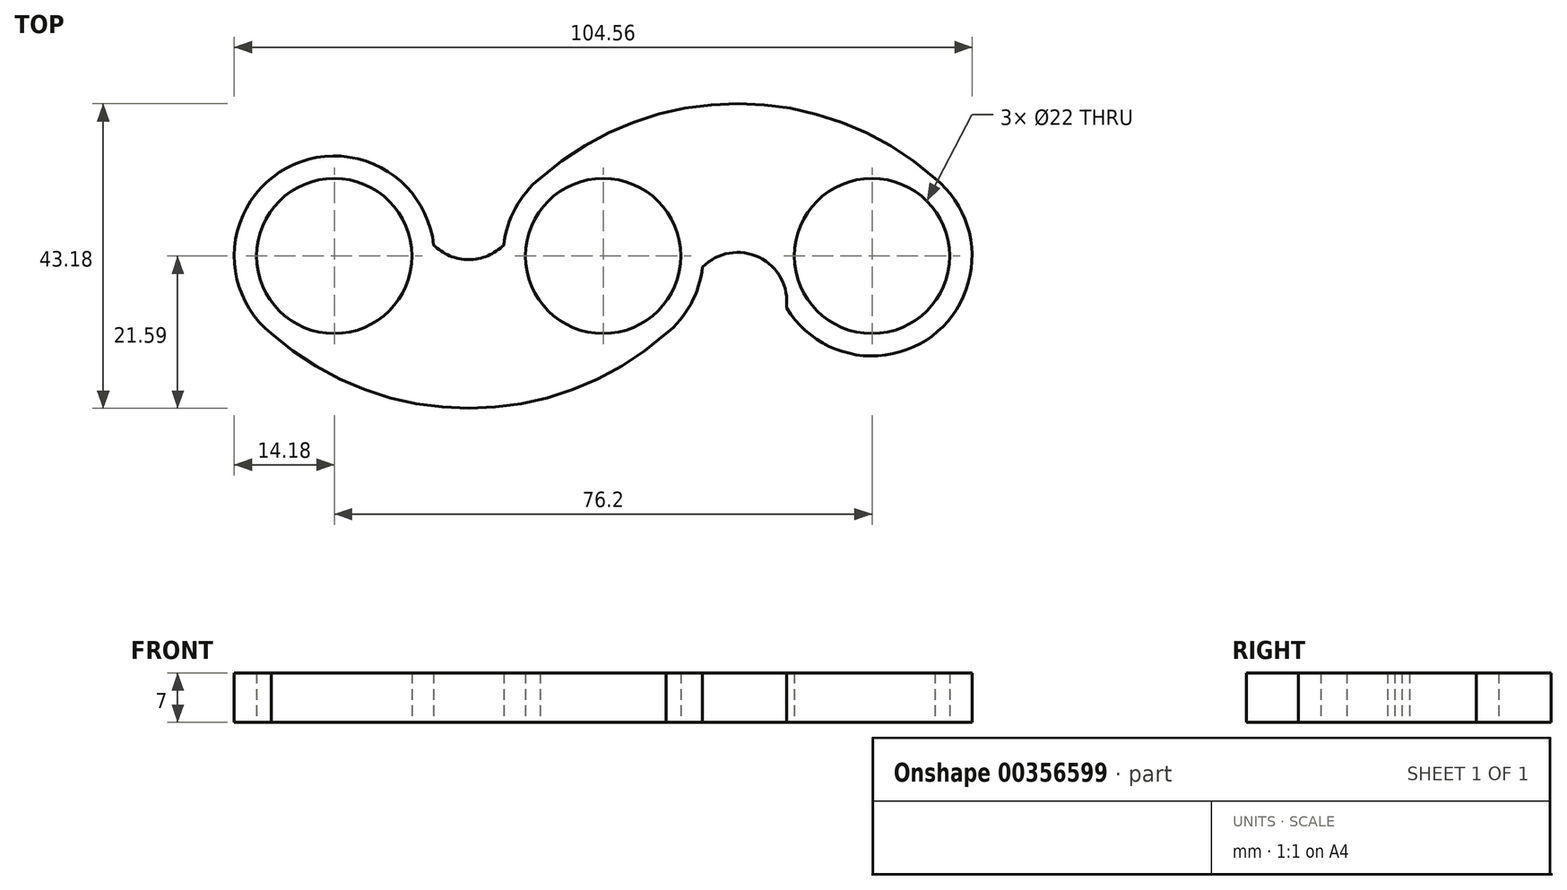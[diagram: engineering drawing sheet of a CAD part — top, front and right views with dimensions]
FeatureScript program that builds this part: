
annotation { "Feature Type Name" : "Feature", "Feature Type Description" : "" }
export const myFeature = defineFeature(function(context is Context, id is Id, definition is map)
    precondition{}
    {
        {
            var Q0;
            Q0=qCreatedBy(makeId("Top.planeOp"),FACE);
            var sketch = newSketch(context, id + "F0", { "sketchPlane" : qUnion([Q0])});
            skCircle(sketch, "E0", {"center": v(0, 0) * mm, "radius": 11 * mm});
            skLineSegment(sketch, "E1", {"start": v(0, 0) * mm, "end": v(-38.1, 0) * mm});
            skLineSegment(sketch, "E2", {"start": v(0, 0) * mm, "end": v(38.1, 0) * mm});
            skCircle(sketch, "E3", {"center": v(-38.1, 0) * mm, "radius": 11 * mm});
            skCircle(sketch, "E4", {"center": v(38.1, 0) * mm, "radius": 11 * mm});
            skCircle(sketch, "E5", {"center": v(-38.1, 0) * mm, "radius": 14.17 * mm});
            skCircle(sketch, "E6", {"center": v(38.1, 0) * mm, "radius": 14.17 * mm});
            skCircle(sketch, "E7", {"center": v(0, 0) * mm, "radius": 14.17 * mm});
            skPoint(sketch, "E8", {"position": v(0, 14.17) * mm});
            skPoint(sketch, "E9", {"position": v(-50.8, 6.3) * mm});
            skPoint(sketch, "E10", {"position": v(-29.16, 11) * mm});
            skPoint(sketch, "E11", {"position": v(-8.94, 11) * mm});
            skPoint(sketch, "E12", {"position": v(-25.97, 7.33) * mm});
            skPoint(sketch, "E13", {"position": v(-12.13, 7.33) * mm});
            skPoint(sketch, "E14", {"position": v(-16.43, 0) * mm});
            skPoint(sketch, "E15", {"position": v(-47.04, -11) * mm});
            skPoint(sketch, "E16", {"position": v(8.94, -11) * mm});
            skPoint(sketch, "E17", {"position": v(-16.44, -21.5) * mm});
            skArc(sketch, "E18", {"start": v(-47.04, -11) * mm, "mid": v(-19.05, -21.59) * mm, "end": v(8.94, -11) * mm});
            skLineSegment(sketch, "E19", {"start": v(0, 55.32) * mm, "end": v(0, -62.03) * mm});
            skPoint(sketch, "E20", {"position": v(16.43, 0) * mm});
            skPoint(sketch, "E21", {"position": v(25.97, -7.34) * mm});
            skPoint(sketch, "E22", {"position": v(12.13, -7.34) * mm});
            skPoint(sketch, "E23", {"position": v(47.04, 11) * mm});
            skPoint(sketch, "E24", {"position": v(16.43, 21.51) * mm});
            skArc(sketch, "E25", {"start": v(47.04, 11) * mm, "mid": v(19.05, 21.6) * mm, "end": v(-8.94, 11) * mm});
            skArc(sketch, "E26", {"start": v(25.97, -7.34) * mm, "mid": v(19.05, 0.5) * mm, "end": v(12.13, -7.34) * mm});
            skArc(sketch, "E27", {"start": v(-25.97, 7.33) * mm, "mid": v(-19.05, -0.5) * mm, "end": v(-12.13, 7.33) * mm});
            skSolve(sketch);
        }
        {
            var Q0;
            Q0=makeQuery(id+"F0.imprint","IMPRINT",FACE,{"disambiguationData":[TD([[makeQuery(id+"F0.imprint","IMPRINT",EDGE,{"derivedFrom":sQuery(id+"F0.wireOp",EDGE,"E4")}),-1.0]])]});
            var Q1;
            {var subQ1=sQuery(id+"F0.wireOp",EDGE,"E2");var subQ5=sQuery(id+"F0.wireOp",EDGE,"E26");var subQ6=makeQuery(id+"F0.imprint","INTERSECT",VERTEX,{"disambiguationData":[OD(0.0)],"derivedFrom":[subQ1,subQ5]});Q1=makeQuery(id+"F0.imprint","IMPRINT",FACE,{"disambiguationData":[TD([[makeQuery(id+"F0.imprint","IMPRINT",EDGE,{"disambiguationData":[TD([[subQ6,1.0]])],"derivedFrom":subQ1}),1.0]])]});}
            var Q2;
            {var subQ1=sQuery(id+"F0.wireOp",EDGE,"E1");var subQ9=sQuery(id+"F0.wireOp",EDGE,"hHHfzR90-xdfu-g8HF-ednO-0jAwHizbKKlp");var subQ12=makeQuery(id+"F0.imprint","INTERSECT",VERTEX,{"disambiguationData":[OD(0.0)],"derivedFrom":[subQ1,subQ9]});Q2=makeQuery(id+"F0.imprint","IMPRINT",FACE,{"disambiguationData":[TD([[makeQuery(id+"F0.imprint","IMPRINT",EDGE,{"disambiguationData":[TD([[subQ12,1.0]])],"derivedFrom":subQ1}),1.0]])]});}
            var Q3;
            Q3=makeQuery(id+"F0.imprint","IMPRINT",FACE,{"disambiguationData":[TD([[makeQuery(id+"F0.imprint","IMPRINT",EDGE,{"derivedFrom":sQuery(id+"F0.wireOp",EDGE,"E3")}),-1.0]])]});
            var Q4;
            {var subQ6=sQuery(id+"F0.wireOp",EDGE,"E2");var subQ7=sQuery(id+"F0.wireOp",EDGE,"E0");var subQ8=makeQuery(id+"F0.imprint","INTERSECT",VERTEX,{"derivedFrom":[subQ7,subQ6]});Q4=makeQuery(id+"F0.imprint","IMPRINT",FACE,{"disambiguationData":[TD([[makeQuery(id+"F0.imprint","IMPRINT",EDGE,{"disambiguationData":[TD([[subQ8,1.0]])],"derivedFrom":subQ7}),-1.0]])]});}
            var Q5;
            {var subQ0=sQuery(id+"F0.wireOp",EDGE,"E1");var subQ1=sQuery(id+"F0.wireOp",EDGE,"E0");var subQ2=makeQuery(id+"F0.imprint","INTERSECT",VERTEX,{"derivedFrom":[subQ1,subQ0]});Q5=makeQuery(id+"F0.imprint","IMPRINT",FACE,{"disambiguationData":[TD([[makeQuery(id+"F0.imprint","IMPRINT",EDGE,{"disambiguationData":[TD([[subQ2,-1.0]])],"derivedFrom":subQ1}),-1.0]])]});}
            var Q6;
            {var subQ6=sQuery(id+"F0.wireOp",EDGE,"E19");var subQ9=sQuery(id+"F0.wireOp",EDGE,"E0");var subQ12=makeQuery(id+"F0.imprint","INTERSECT",VERTEX,{"disambiguationData":[OD(0.0)],"derivedFrom":[subQ9,subQ6]});Q6=makeQuery(id+"F0.imprint","IMPRINT",FACE,{"disambiguationData":[TD([[makeQuery(id+"F0.imprint","IMPRINT",EDGE,{"disambiguationData":[TD([[subQ12,-1.0]])],"derivedFrom":subQ9}),-1.0]])]});}
            var Q7;
            {var subQ0=sQuery(id+"F0.wireOp",EDGE,"E26");var subQ1=sQuery(id+"F0.wireOp",EDGE,"E2");var subQ2=makeQuery(id+"F0.imprint","INTERSECT",VERTEX,{"disambiguationData":[OD(0.0)],"derivedFrom":[subQ1,subQ0]});Q7=makeQuery(id+"F0.imprint","IMPRINT",FACE,{"disambiguationData":[TD([[makeQuery(id+"F0.imprint","IMPRINT",EDGE,{"disambiguationData":[TD([[subQ2,1.0]])],"derivedFrom":subQ1}),-1.0]])]});}
            var Q8;
            {var subQ0=sQuery(id+"F0.wireOp",EDGE,"E19");var subQ1=sQuery(id+"F0.wireOp",EDGE,"E0");var subQ2=makeQuery(id+"F0.imprint","INTERSECT",VERTEX,{"disambiguationData":[OD(0.0)],"derivedFrom":[subQ1,subQ0]});Q8=makeQuery(id+"F0.imprint","IMPRINT",FACE,{"disambiguationData":[TD([[makeQuery(id+"F0.imprint","IMPRINT",EDGE,{"disambiguationData":[TD([[subQ2,1.0]])],"derivedFrom":subQ1}),-1.0]])]});}
            var Q9;
            {var subQ0=sQuery(id+"F0.wireOp",EDGE,"E25");var subQ1=sQuery(id+"F0.wireOp",EDGE,"E7");var subQ2=makeQuery(id+"F0.imprint","INTERSECT",VERTEX,{"disambiguationData":[OD(1.0)],"derivedFrom":[subQ1,subQ0]});Q9=makeQuery(id+"F0.imprint","IMPRINT",FACE,{"disambiguationData":[TD([[makeQuery(id+"F0.imprint","IMPRINT",EDGE,{"disambiguationData":[TD([[subQ2,1.0]])],"derivedFrom":subQ1}),-1.0]])]});}
            var Q10;
            {var subQ0=sQuery(id+"F0.wireOp",EDGE,"hHHfzR90-xdfu-g8HF-ednO-0jAwHizbKKlp");var subQ1=sQuery(id+"F0.wireOp",EDGE,"E1");var subQ2=makeQuery(id+"F0.imprint","INTERSECT",VERTEX,{"disambiguationData":[OD(0.0)],"derivedFrom":[subQ1,subQ0]});Q10=makeQuery(id+"F0.imprint","IMPRINT",FACE,{"disambiguationData":[TD([[makeQuery(id+"F0.imprint","IMPRINT",EDGE,{"disambiguationData":[TD([[subQ2,1.0]])],"derivedFrom":subQ1}),-1.0]])]});}
            var Q11;
            {var subQ0=sQuery(id+"F0.wireOp",EDGE,"hHHfzR90-xdfu-g8HF-ednO-0jAwHizbKKlp");var subQ1=sQuery(id+"F0.wireOp",EDGE,"E1");var subQ2=makeQuery(id+"F0.imprint","INTERSECT",VERTEX,{"disambiguationData":[OD(1.0)],"derivedFrom":[subQ1,subQ0]});Q11=makeQuery(id+"F0.imprint","IMPRINT",FACE,{"disambiguationData":[TD([[makeQuery(id+"F0.imprint","IMPRINT",EDGE,{"disambiguationData":[TD([[subQ2,-1.0]])],"derivedFrom":subQ1}),-1.0]])]});}
            var Q12;
            {var subQ0=sQuery(id+"F0.wireOp",EDGE,"E18");var subQ1=sQuery(id+"F0.wireOp",EDGE,"E7");var subQ2=makeQuery(id+"F0.imprint","INTERSECT",VERTEX,{"disambiguationData":[OD(1.0)],"derivedFrom":[subQ1,subQ0]});Q12=makeQuery(id+"F0.imprint","IMPRINT",FACE,{"disambiguationData":[TD([[makeQuery(id+"F0.imprint","IMPRINT",EDGE,{"disambiguationData":[TD([[subQ2,1.0]])],"derivedFrom":subQ1}),-1.0]])]});}
            var Q13;
            {var subQ0=sQuery(id+"F0.wireOp",EDGE,"E26");var subQ1=sQuery(id+"F0.wireOp",EDGE,"E2");var subQ2=makeQuery(id+"F0.imprint","INTERSECT",VERTEX,{"disambiguationData":[OD(1.0)],"derivedFrom":[subQ1,subQ0]});Q13=makeQuery(id+"F0.imprint","IMPRINT",FACE,{"disambiguationData":[TD([[makeQuery(id+"F0.imprint","IMPRINT",EDGE,{"disambiguationData":[TD([[subQ2,-1.0]])],"derivedFrom":subQ1}),-1.0]])]});}
            var Q14;
            {var subQ1=sQuery(id+"F0.wireOp",EDGE,"E1");var subQ5=sQuery(id+"F0.wireOp",EDGE,"E27");var subQ6=makeQuery(id+"F0.imprint","INTERSECT",VERTEX,{"disambiguationData":[OD(0.0)],"derivedFrom":[subQ1,subQ5]});Q14=makeQuery(id+"F0.imprint","IMPRINT",FACE,{"disambiguationData":[TD([[makeQuery(id+"F0.imprint","IMPRINT",EDGE,{"disambiguationData":[TD([[subQ6,1.0]])],"derivedFrom":subQ1}),1.0]])]});}
            var Q15;
            {var subQ0=sQuery(id+"F0.wireOp",EDGE,"E26");var subQ1=sQuery(id+"F0.wireOp",EDGE,"E7");var subQ2=makeQuery(id+"F0.imprint","INTERSECT",VERTEX,{"disambiguationData":[OD(0.0)],"derivedFrom":[subQ1,subQ0]});Q15=makeQuery(id+"F0.imprint","IMPRINT",FACE,{"disambiguationData":[TD([[makeQuery(id+"F0.imprint","IMPRINT",EDGE,{"disambiguationData":[TD([[subQ2,-1.0]])],"derivedFrom":subQ1}),1.0]])]});}
            var Q16;
            {var subQ0=sQuery(id+"F0.wireOp",EDGE,"E26");var subQ1=sQuery(id+"F0.wireOp",EDGE,"E6");var subQ2=makeQuery(id+"F0.imprint","INTERSECT",VERTEX,{"disambiguationData":[OD(0.0)],"derivedFrom":[subQ1,subQ0]});Q16=makeQuery(id+"F0.imprint","IMPRINT",FACE,{"disambiguationData":[TD([[makeQuery(id+"F0.imprint","IMPRINT",EDGE,{"disambiguationData":[TD([[subQ2,1.0]])],"derivedFrom":subQ1}),1.0]])]});}
            var Q17;
            {var subQ0=sQuery(id+"F0.wireOp",EDGE,"E27");var subQ1=sQuery(id+"F0.wireOp",EDGE,"E1");var subQ2=makeQuery(id+"F0.imprint","INTERSECT",VERTEX,{"disambiguationData":[OD(0.0)],"derivedFrom":[subQ1,subQ0]});Q17=makeQuery(id+"F0.imprint","IMPRINT",FACE,{"disambiguationData":[TD([[makeQuery(id+"F0.imprint","IMPRINT",EDGE,{"disambiguationData":[TD([[subQ2,1.0]])],"derivedFrom":subQ1}),-1.0]])]});}
            var Q18;
            {var subQ0=sQuery(id+"F0.wireOp",EDGE,"E27");var subQ1=sQuery(id+"F0.wireOp",EDGE,"E7");var subQ2=makeQuery(id+"F0.imprint","INTERSECT",VERTEX,{"disambiguationData":[OD(0.0)],"derivedFrom":[subQ1,subQ0]});Q18=makeQuery(id+"F0.imprint","IMPRINT",FACE,{"disambiguationData":[TD([[makeQuery(id+"F0.imprint","IMPRINT",EDGE,{"disambiguationData":[TD([[subQ2,-1.0]])],"derivedFrom":subQ1}),1.0]])]});}
            var Q19;
            {var subQ0=sQuery(id+"F0.wireOp",EDGE,"E27");var subQ1=sQuery(id+"F0.wireOp",EDGE,"E1");var subQ2=makeQuery(id+"F0.imprint","INTERSECT",VERTEX,{"disambiguationData":[OD(1.0)],"derivedFrom":[subQ1,subQ0]});Q19=makeQuery(id+"F0.imprint","IMPRINT",FACE,{"disambiguationData":[TD([[makeQuery(id+"F0.imprint","IMPRINT",EDGE,{"disambiguationData":[TD([[subQ2,-1.0]])],"derivedFrom":subQ1}),-1.0]])]});}
            var Q20;
            {var subQ0=sQuery(id+"F0.wireOp",EDGE,"E27");var subQ1=sQuery(id+"F0.wireOp",EDGE,"E5");var subQ2=makeQuery(id+"F0.imprint","INTERSECT",VERTEX,{"disambiguationData":[OD(0.0)],"derivedFrom":[subQ1,subQ0]});Q20=makeQuery(id+"F0.imprint","IMPRINT",FACE,{"disambiguationData":[TD([[makeQuery(id+"F0.imprint","IMPRINT",EDGE,{"disambiguationData":[TD([[subQ2,1.0]])],"derivedFrom":subQ1}),1.0]])]});}
            extrude(context, id + "F1", {"entities" : qUnion([Q0, Q1, Q2, Q3, Q4, Q5, Q6, Q7, Q8, Q9, Q10, Q11, Q12, Q13, Q14, Q15, Q16, Q17, Q18, Q19, Q20]), "depth" : 7 * mm});
        }
    });
